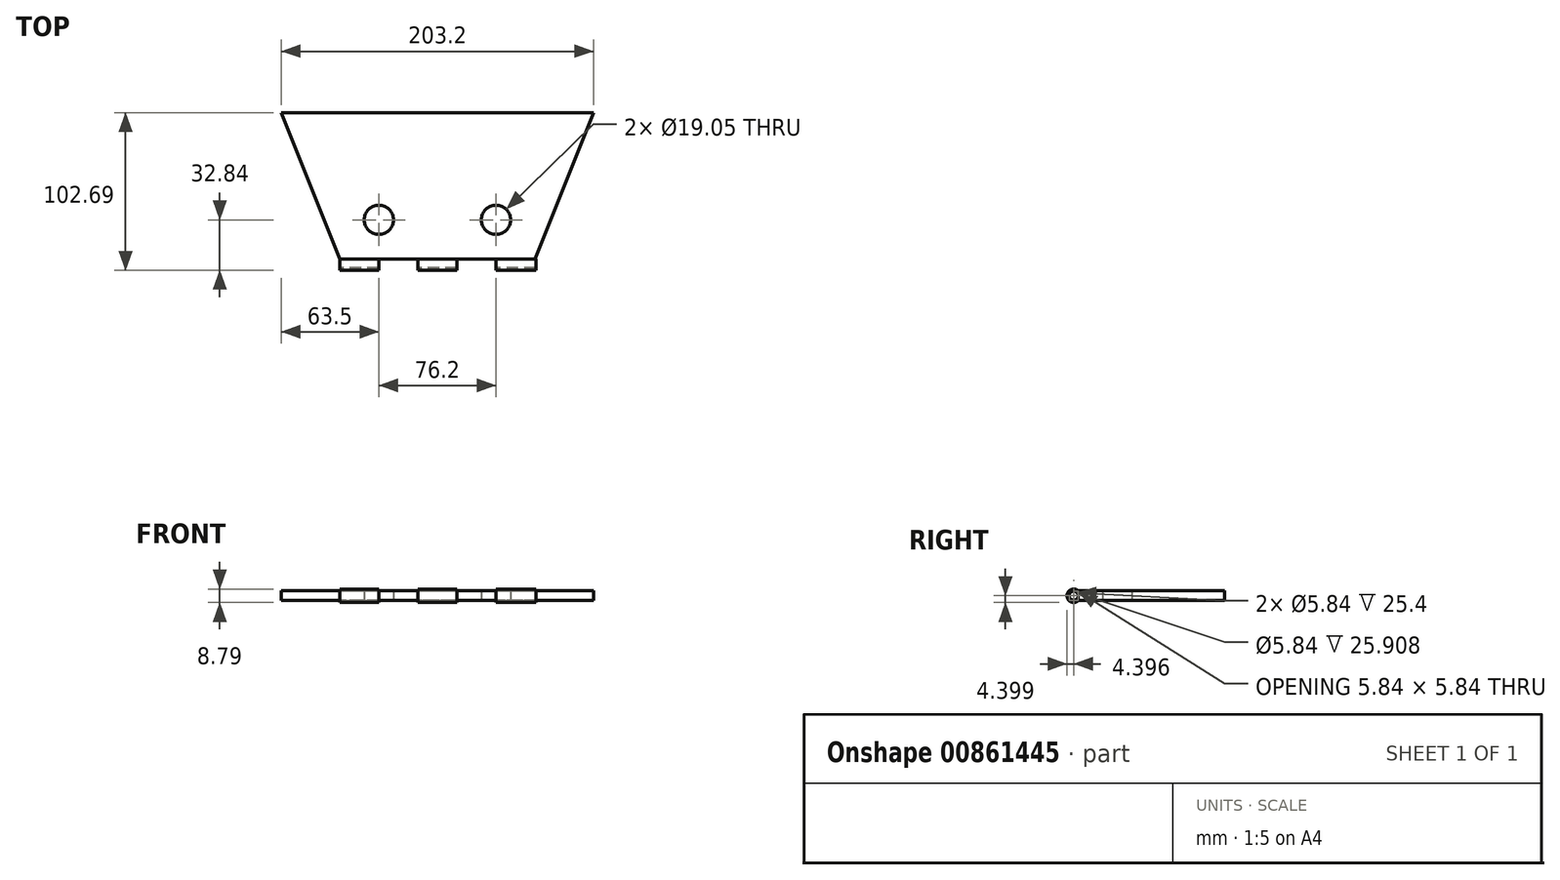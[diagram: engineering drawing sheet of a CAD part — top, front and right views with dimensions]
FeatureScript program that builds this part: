
annotation { "Feature Type Name" : "Feature", "Feature Type Description" : "" }
export const myFeature = defineFeature(function(context is Context, id is Id, definition is map)
    precondition{}
    {
        {
            var Q0;
            Q0=qCreatedBy(makeId("Top.planeOp"),FACE);
            var sketch = newSketch(context, id + "F0", { "sketchPlane" : qUnion([Q0])});
            skLineSegment(sketch, "E0", {"start": v(-63.5, 95.25) * mm, "end": v(-25.4, 0) * mm});
            skLineSegment(sketch, "E1", {"start": v(-25.4, 0) * mm, "end": v(101.6, 0) * mm});
            skLineSegment(sketch, "E2", {"start": v(101.6, 0) * mm, "end": v(139.7, 95.25) * mm});
            skLineSegment(sketch, "E3", {"start": v(139.7, 95.25) * mm, "end": v(-63.5, 95.25) * mm});
            skSolve(sketch);
        }
        {
            var Q0;
            Q0=makeQuery(id+"F0.imprint","IMPRINT",FACE,{"disambiguationData":[TD([[makeQuery(id+"F0.imprint","IMPRINT",EDGE,{"derivedFrom":sQuery(id+"F0.wireOp",EDGE,"E0")}),1.0]])]});
            extrude(context, id + "F1", {"entities" : qUnion([Q0]), "depth" : 6.35 * mm, "offsetDistance" : 25.4 * mm});
        }
        {
            var Q0;
            Q0=qCreatedBy(makeId("Right.planeOp"),FACE);
            var sketch = newSketch(context, id + "F2", { "sketchPlane" : qUnion([Q0])});
            skArc(sketch, "E4", {"start": v(0, 6.34) * mm, "mid": v(-7.44, 3.17) * mm, "end": v(0, 0) * mm});
            skCircle(sketch, "E5", {"center": v(-3.04, 3.17) * mm, "radius": 2.92 * mm});
            skLineSegment(sketch, "E6", {"start": v(0, 6.34) * mm, "end": v(0, 0) * mm});
            skSolve(sketch);
        }
        {
            var Q0;
            Q0 = qSketchRegion(id + "F2", true);
            var Q1;
            Q1=makeQuery(id+"F2.imprint","IMPRINT",FACE,{"disambiguationData":[TD([[makeQuery(id+"F2.imprint","IMPRINT",EDGE,{"derivedFrom":sQuery(id+"F2.wireOp",EDGE,"J6r9Z09W-sDtT-4e2n-wa94-bA2nsMSwHwn8")}),-1.0]])]});
            extrude(context, id + "F3", {"entities" : qUnion([Q0, Q1]), "operationType" : NewBodyOperationType.ADD, "depth" : 102.1 * mm, "offsetDistance" : 25.4 * mm, "hasSecondDirection" : true, "secondDirectionOppositeDirection" : true, "secondDirectionDepth" : 25.4 * mm});
        }
        {
            var Q0;
            Q0=makeQuery(id+"F1.opExtrude","CAP_FACE",FACE,{"disambiguationData":[OSD([sQuery(id+"F0.wireOp",EDGE,"E0"),sQuery(id+"F0.wireOp",EDGE,"E1"),sQuery(id+"F0.wireOp",EDGE,"E2"),sQuery(id+"F0.wireOp",EDGE,"E3")])],"isStart":true});
            var sketch = newSketch(context, id + "F4", { "sketchPlane" : qUnion([Q0])});
            skSolve(sketch);
        }
        {
            var Q0;
            {var subQ10=sQuery(id+"F0.wireOp",EDGE,"E0");Q0=makeQuery(id+"F4.imprint","IMPRINT",FACE,{"disambiguationData":[TD([[makeQuery(id+"F4.imprint","IMPRINT",EDGE,{"derivedFrom":makeQuery(id+"F1.opExtrude","CAP_EDGE",EDGE,{"disambiguationData":[OSD([subQ10])],"isStart":true})}),-1.0]])]});}
            var sketch = newSketch(context, id + "F5", { "sketchPlane" : qUnion([Q0])});
            skLineSegment(sketch, "E7", {"start": v(-35.9, -25.4) * mm, "end": v(111.76, -25.4) * mm});
            skCircle(sketch, "E8", {"center": v(0, -25.4) * mm, "radius": 9.53 * mm});
            skCircle(sketch, "E9", {"center": v(76.2, -25.4) * mm, "radius": 4.5 * mm});
            skSolve(sketch);
        }
        {
            var Q0;
            Q0=sQuery(id+"F5.wireOp",VERTEX,"E8.center");
            var Q1;
            Q1=sQuery(id+"F5.wireOp",VERTEX,"E9.center");
            var Q2;
            Q2=makeQuery(id+"F1.opExtrude","SWEPT_BODY",BODY,{"disambiguationData":[OSD([sQuery(id+"F0.wireOp",EDGE,"E0"),sQuery(id+"F0.wireOp",EDGE,"E1"),sQuery(id+"F0.wireOp",EDGE,"E2"),sQuery(id+"F0.wireOp",EDGE,"E3")])]});
            hole(context, id + "F6", {"style" : HoleStyle.SIMPLE, "endStyle" : HoleEndStyle.THROUGH, "holeDiameter" : 19.05 * mm, "majorDiameter" : 6.35 * mm, "isTappedThrough" : true, "tappedDepth" : 12.7 * mm, "tapClearance" : 3, "locations" : qUnion([Q0, Q1]), "scope" : qUnion([Q2])});
        }
        {
            var Q0;
            Q0=makeQuery(id+"F1.opExtrude","CAP_FACE",FACE,{"disambiguationData":[OSD([sQuery(id+"F0.wireOp",EDGE,"E0"),sQuery(id+"F0.wireOp",EDGE,"E1"),sQuery(id+"F0.wireOp",EDGE,"E2"),sQuery(id+"F0.wireOp",EDGE,"E3")])],"isStart":false});
            var sketch = newSketch(context, id + "F7", { "sketchPlane" : qUnion([Q0])});
            skLineSegment(sketch, "E10.bottom", {"start": v(0, 0) * mm, "end": v(25.4, 0) * mm});
            skLineSegment(sketch, "E10.top", {"start": v(0, -8.6) * mm, "end": v(25.4, -8.6) * mm});
            skLineSegment(sketch, "E10.left", {"start": v(0, 0) * mm, "end": v(0, -8.6) * mm});
            skLineSegment(sketch, "E10.right", {"start": v(25.4, 0) * mm, "end": v(25.4, -8.6) * mm});
            skLineSegment(sketch, "E11.bottom", {"start": v(50.8, 0) * mm, "end": v(76.2, 0) * mm});
            skLineSegment(sketch, "E11.top", {"start": v(50.8, -11.81) * mm, "end": v(76.2, -11.81) * mm});
            skLineSegment(sketch, "E11.left", {"start": v(50.8, 0) * mm, "end": v(50.8, -11.81) * mm});
            skLineSegment(sketch, "E11.right", {"start": v(76.2, 0) * mm, "end": v(76.2, -11.81) * mm});
            skSolve(sketch);
        }
        {
            var Q0;
            Q0=makeQuery(id+"F7.imprint","IMPRINT",FACE,{"disambiguationData":[TD([[makeQuery(id+"F7.imprint","IMPRINT",EDGE,{"derivedFrom":sQuery(id+"F7.wireOp",EDGE,"E10.bottom")}),-1.0]])]});
            var Q1;
            Q1=makeQuery(id+"F7.imprint","IMPRINT",FACE,{"disambiguationData":[TD([[makeQuery(id+"F7.imprint","IMPRINT",EDGE,{"derivedFrom":sQuery(id+"F7.wireOp",EDGE,"E11.bottom")}),-1.0]])]});
            extrude(context, id + "F8", {"entities" : qUnion([Q0, Q1]), "operationType" : NewBodyOperationType.REMOVE, "endBound" : BoundingType.SYMMETRIC, "oppositeDirection" : true, "depth" : 25.4 * mm, "hasOffset" : true, "offsetDistance" : 25.4 * mm});
        }
    });
